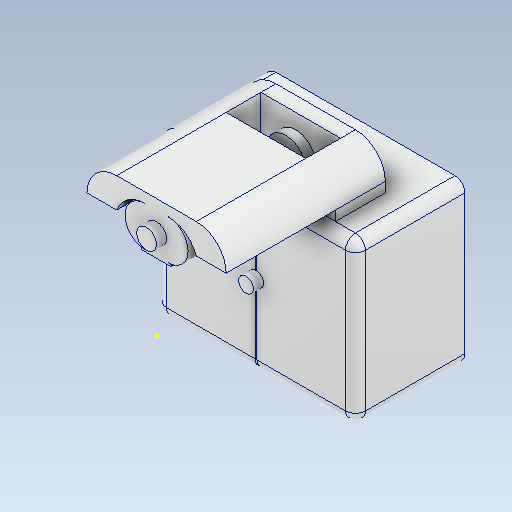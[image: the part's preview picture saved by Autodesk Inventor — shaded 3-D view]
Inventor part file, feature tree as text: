
AUTODESK INVENTOR PART (.ipt)
format: ipt  version: 2021 (Build 250183000, 183)  size: 336,896 bytes
history: native  units: mm
features: sketch x27, other x3, plane x2
ambient origin geometry x8: Origin, YZ Plane, XZ Plane, XY Plane, X Axis, Y Axis, Z Axis, Center Point
bodies: Solid1 (feature_tree)
feature tree (32):
  other  "Gear and handle.ipt"
  other  "Solid1::Gear and handle.ipt"
  other  "TaggingFeature1"
  sketch  "Sketch1"  dims[d0=10.0mm]
  sketch  "Sketch2"
  sketch  "Sketch3"
  sketch  "Sketch4"
  sketch  "Sketch5"
  sketch  "Sketch6"
  sketch  "Sketch7"
  sketch  "Sketch8"
  sketch  "Sketch9"
  sketch  "Sketch10"
  sketch  "Sketch11"
  sketch  "Sketch12"
  sketch  "Sketch14"
  sketch  "Sketch15"
  sketch  "Sketch16"
  sketch  "Sketch17"
  sketch  "Sketch18"
  sketch  "Sketch19"
  sketch  "Sketch24"
  sketch  "Sketch25"
  sketch  "Sketch26"
  sketch  "Sketch29"
  sketch  "Sketch30"
  sketch  "Sketch31"
  sketch  "Sketch32"
  sketch  "Sketch33"
  sketch  "Sketch34"
  plane  "Work Plane1"
  plane  "Work Plane2"
